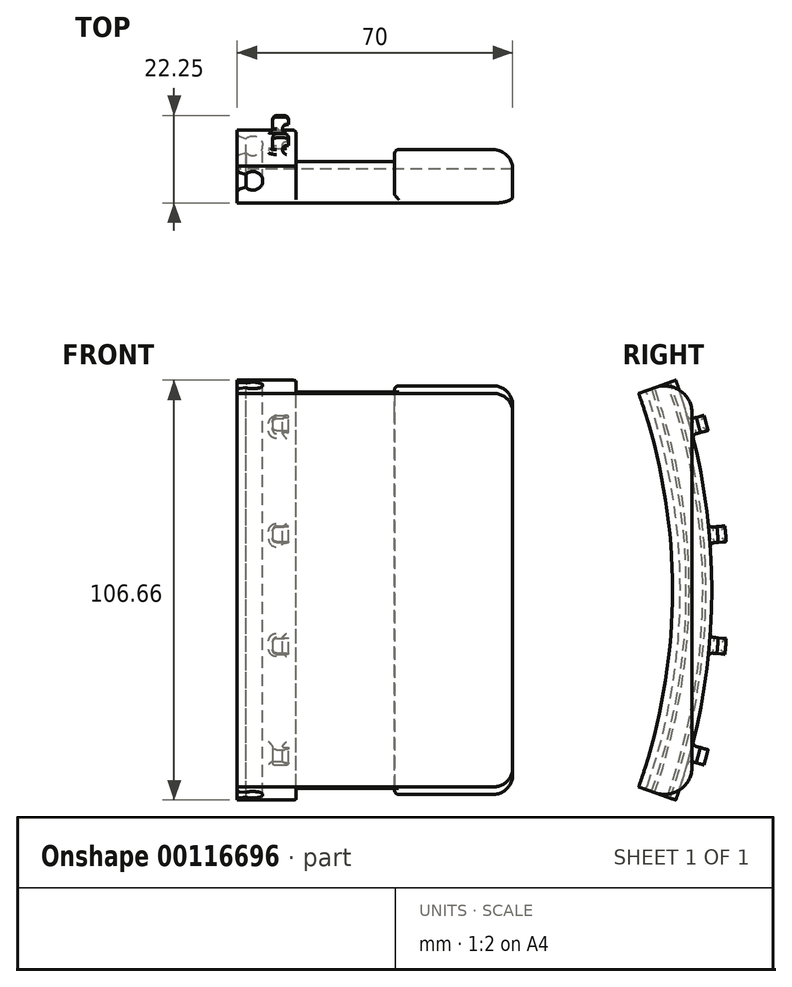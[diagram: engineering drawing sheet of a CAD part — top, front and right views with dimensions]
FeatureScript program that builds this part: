
annotation { "Feature Type Name" : "Feature", "Feature Type Description" : "" }
export const myFeature = defineFeature(function(context is Context, id is Id, definition is map)
    precondition{}
    {
        {
            var Q0;
            Q0=qCreatedBy(makeId("Right.planeOp"),FACE);
            var sketch = newSketch(context, id + "F0", { "sketchPlane" : qUnion([Q0])});
            skArc(sketch, "E0", {"start": v(141.42, -50) * mm, "mid": v(147.84, -25.37) * mm, "end": v(150, 0) * mm});
            skLineSegment(sketch, "E1", {"start": v(155, 0) * mm, "end": v(150, 0) * mm, "construction": true});
            skLineSegment(sketch, "E2", {"start": v(0, 0) * mm, "end": v(141.42, -50) * mm, "construction": true});
            skLineSegment(sketch, "E3", {"start": v(141.42, -50) * mm, "end": v(155, -54.8) * mm});
            skLineSegment(sketch, "E4", {"start": v(155, -54.8) * mm, "end": v(155, 0) * mm});
            skLineSegment(sketch, "E5.MirrorCS", {"start": v(155, 54.8) * mm, "end": v(155, 0) * mm});
            skLineSegment(sketch, "E6.MirrorCS", {"start": v(141.42, 50) * mm, "end": v(155, 54.8) * mm});
            skArc(sketch, "E7.MirrorCS", {"start": v(141.42, 50) * mm, "mid": v(147.84, 25.37) * mm, "end": v(150, 0) * mm});
            skSolve(sketch);
        }
        {
            var Q0;
            Q0 = qSketchRegion(id + "F0", true);
            extrude(context, id + "F1", {"entities" : qUnion([Q0]), "depth" : 30 * mm});
        }
        {
            var Q0;
            Q0=makeQuery(id+"F1.opExtrude","CAP_FACE",FACE,{"disambiguationData":[OSD([sQuery(id+"F0.wireOp",EDGE,"E0"),sQuery(id+"F0.wireOp",EDGE,"E3"),sQuery(id+"F0.wireOp",EDGE,"E4"),sQuery(id+"F0.wireOp",EDGE,"E5.MirrorCS"),sQuery(id+"F0.wireOp",EDGE,"E6.MirrorCS"),sQuery(id+"F0.wireOp",EDGE,"E7.MirrorCS")])],"isStart":true});
            var sketch = newSketch(context, id + "F2", { "sketchPlane" : qUnion([Q0])});
            skArc(sketch, "E8.0", {"start": v(-141.42, -50) * mm, "mid": v(-150, 0) * mm, "end": v(-141.42, 50) * mm});
            skArc(sketch, "E9.0", {"start": v(-143.3, -50.67) * mm, "mid": v(-152, 0) * mm, "end": v(-143.3, 50.67) * mm});
            skLineSegment(sketch, "E10", {"start": v(-141.42, -50) * mm, "end": v(-143.3, -50.67) * mm});
            skLineSegment(sketch, "E11", {"start": v(-141.42, 50) * mm, "end": v(-143.3, 50.67) * mm});
            skSolve(sketch);
        }
        {
            var Q0;
            Q0 = qSketchRegion(id + "F2", true);
            extrude(context, id + "F3", {"entities" : qUnion([Q0]), "operationType" : NewBodyOperationType.ADD, "depth" : 40 * mm});
        }
        {
            var Q0;
            Q0=makeQuery(id+"F3.boolean.opBoolean","MERGE",FACE,{"derivedFrom":[makeQuery(id+"F1.opExtrude","SWEPT_FACE",FACE,{"disambiguationData":[OSD([sQuery(id+"F0.wireOp",EDGE,"E3")])]}),makeQuery(id+"F3.opExtrude","SWEPT_FACE",FACE,{"disambiguationData":[OSD([sQuery(id+"F2.wireOp",EDGE,"E10")])]})]});
            var sketch = newSketch(context, id + "F4", { "sketchPlane" : qUnion([Q0])});
            skLineSegment(sketch, "E12.bottom", {"start": v(-40, -152) * mm, "end": v(-25, -152) * mm});
            skLineSegment(sketch, "E12.top", {"start": v(-40, -160) * mm, "end": v(-31, -160) * mm});
            skLineSegment(sketch, "E12.left", {"start": v(-40, -152) * mm, "end": v(-40, -153.48) * mm});
            skLineSegment(sketch, "E12.right", {"start": v(-25, -152) * mm, "end": v(-25, -160) * mm});
            skArc(sketch, "E13", {"start": v(-37.81, -157.72) * mm, "mid": v(-33.5, -156) * mm, "end": v(-37.81, -154.28) * mm});
            skPoint(sketch, "E13.centerSnap0", {"position": v(-25, -85) * mm});
            skPoint(sketch, "E13.centerSnap1", {"position": v(-40, -156) * mm});
            skLineSegment(sketch, "E14", {"start": v(-37.81, -157.72) * mm, "end": v(-40, -158.52) * mm});
            skLineSegment(sketch, "E15", {"start": v(-36, -156) * mm, "end": v(-40, -156) * mm, "construction": true});
            skLineSegment(sketch, "E16.MirrorCS", {"start": v(-37.81, -154.28) * mm, "end": v(-40, -153.48) * mm});
            skLineSegment(sketch, "E17.trimOffspring", {"start": v(-40, -158.52) * mm, "end": v(-40, -160) * mm});
            skLineSegment(sketch, "E18", {"start": v(-31, -160) * mm, "end": v(-31, -164.13) * mm});
            skLineSegment(sketch, "E19", {"start": v(-31, -164.13) * mm, "end": v(-27, -164.13) * mm});
            skLineSegment(sketch, "E20", {"start": v(-27, -164.13) * mm, "end": v(-27, -162.1) * mm});
            skLineSegment(sketch, "E21", {"start": v(-27, -162.1) * mm, "end": v(-28.5, -162.1) * mm});
            skLineSegment(sketch, "E22", {"start": v(-28.5, -162.1) * mm, "end": v(-28.5, -160) * mm});
            skLineSegment(sketch, "E23.trimOffspring", {"start": v(-28.5, -160) * mm, "end": v(-25, -160) * mm});
            skSolve(sketch);
        }
        {
            var Q0;
            Q0=makeQuery(id+"F4.imprint","IMPRINT",FACE,{"disambiguationData":[TD([[makeQuery(id+"F4.imprint","IMPRINT",EDGE,{"derivedFrom":sQuery(id+"F4.wireOp",EDGE,"E12.bottom")}),-1.0]])]});
            var Q1;
            Q1=makeQuery(id+"F3.opExtrude","CAP_EDGE",EDGE,{"disambiguationData":[OSD([sQuery(id+"F2.wireOp",EDGE,"E9.0")])],"isStart":false});
            sweep(context, id + "F5", {"operationType" : NewBodyOperationType.ADD, "profiles" : qUnion([Q0]), "path" : qUnion([Q1])});
        }
        {
            var Q0;
            Q0=makeQuery(id+"F1.opExtrude","SWEPT_EDGE",EDGE,{"disambiguationData":[OSD([sQuery(id+"F0.wireOp",EDGE,"E3"),sQuery(id+"F0.wireOp",EDGE,"E4")])]});
            var Q1;
            Q1=makeQuery(id+"F1.opExtrude","SWEPT_EDGE",EDGE,{"disambiguationData":[OSD([sQuery(id+"F0.wireOp",EDGE,"E5.MirrorCS"),sQuery(id+"F0.wireOp",EDGE,"E6.MirrorCS")])]});
            fillet(context, id + "F6", {"entities" : qUnion([Q0, Q1]), "radius" : 7 * mm, "tangentPropagation" : true, "allowEdgeOverflow" : false});
        }
        {
            var Q0;
            Q0=qCreatedBy(makeId("Right.planeOp"),FACE);
            cPlane(context, id + "F7", {"entities" : qUnion([Q0]), "cplaneType" : CPlaneType.OFFSET, "offset" : 35 * mm, "oppositeDirection" : true, "width" : 150 * mm, "height" : 150 * mm});
        }
        {
            var Q0;
            Q0=makeQuery(id+"F5.opSweep","SWEPT_FACE",FACE,{"disambiguationData":[OSD([sQuery(id+"F2.wireOp",EDGE,"E9.0"),sQuery(id+"F4.wireOp",EDGE,"E18")])]});
            var sketch = newSketch(context, id + "F8", { "sketchPlane" : qUnion([Q0])});
            skPoint(sketch, "E24.orphan", {"position": v(-150.85, 53.33) * mm});
            skLineSegment(sketch, "E25.MirrorCS", {"start": v(-164.3, 46.1) * mm, "end": v(-160.48, 58.7) * mm});
            skLineSegment(sketch, "E26.MirrorCS", {"start": v(-168.24, 12.71) * mm, "end": v(-159.55, 11.95) * mm});
            skLineSegment(sketch, "E27.MirrorCS", {"start": v(-159.07, 15.92) * mm, "end": v(-167.49, 16.66) * mm});
            skLineSegment(sketch, "E28.MirrorCS", {"start": v(-153.92, 43.31) * mm, "end": v(-164.3, 46.1) * mm});
            skLineSegment(sketch, "E29", {"start": v(0, 0) * mm, "end": v(-188.34, 50.47) * mm, "construction": true});
            skLineSegment(sketch, "E30", {"start": v(0, 0) * mm, "end": v(-190.07, 0) * mm, "construction": true});
            skLineSegment(sketch, "E31", {"start": v(0, 0) * mm, "end": v(-193.8, 16.95) * mm, "construction": true});
            skLineSegment(sketch, "E32", {"start": v(-155.05, 39.48) * mm, "end": v(-164.01, 41.88) * mm});
            skLineSegment(sketch, "E33.trimOffspring", {"start": v(-164.01, 41.88) * mm, "end": v(-167.49, 16.66) * mm});
            skArc(sketch, "E34.0", {"start": v(-150.85, -53.33) * mm, "mid": v(-152.52, -48.36) * mm, "end": v(-154.02, -43.34) * mm});
            skLineSegment(sketch, "E35", {"start": v(-150.85, 53.33) * mm, "end": v(-160.48, 58.7) * mm});
            skArc(sketch, "E36.trimOffspring", {"start": v(-154.02, 43.34) * mm, "mid": v(-152.52, 48.36) * mm, "end": v(-150.85, 53.33) * mm});
            skArc(sketch, "E37.trimOffspring", {"start": v(-159.2, 15.94) * mm, "mid": v(-157.57, 27.78) * mm, "end": v(-155.05, 39.48) * mm});
            skLineSegment(sketch, "E38", {"start": v(-168.24, 12.71) * mm, "end": v(-168.24, 0) * mm});
            skLineSegment(sketch, "E39.MirrorCS", {"start": v(-155.05, -39.48) * mm, "end": v(-164.01, -41.88) * mm});
            skLineSegment(sketch, "E40.MirrorCS", {"start": v(-150.85, -53.33) * mm, "end": v(-160.48, -58.7) * mm});
            skLineSegment(sketch, "E41.MirrorCS", {"start": v(-164.3, -46.1) * mm, "end": v(-160.48, -58.7) * mm});
            skLineSegment(sketch, "E42.MirrorCS", {"start": v(-168.24, -12.71) * mm, "end": v(-159.55, -11.95) * mm});
            skLineSegment(sketch, "E43.MirrorCS", {"start": v(-153.92, -43.31) * mm, "end": v(-164.3, -46.1) * mm});
            skPoint(sketch, "E44.MirrorP", {"position": v(-150.85, -53.33) * mm});
            skArc(sketch, "E45.MirrorCS", {"start": v(-154.02, -43.34) * mm, "mid": v(-152.52, -48.36) * mm, "end": v(-150.85, -53.33) * mm});
            skLineSegment(sketch, "E46.MirrorCS", {"start": v(-168.24, -12.71) * mm, "end": v(-168.24, 0) * mm});
            skLineSegment(sketch, "E47.MirrorCS", {"start": v(-159.07, -15.92) * mm, "end": v(-167.49, -16.66) * mm});
            skArc(sketch, "E48.MirrorCS", {"start": v(-159.2, -15.94) * mm, "mid": v(-157.57, -27.78) * mm, "end": v(-155.05, -39.48) * mm});
            skLineSegment(sketch, "E49.MirrorCS", {"start": v(-164.01, -41.88) * mm, "end": v(-167.49, -16.66) * mm});
            skArc(sketch, "E50.trimOffspring", {"start": v(-159.55, -11.95) * mm, "mid": v(-160, 0) * mm, "end": v(-159.55, 11.95) * mm});
            skArc(sketch, "E51.trimOffspring", {"start": v(-155.05, -39.48) * mm, "mid": v(-157.57, -27.78) * mm, "end": v(-159.2, -15.94) * mm});
            skSolve(sketch);
        }
        {
            var Q0;
            Q0 = qSketchRegion(id + "F8", true);
            var Q1;
            Q1=makeQuery(id+"F5.opSweep","SWEPT_FACE",FACE,{"disambiguationData":[OSD([sQuery(id+"F2.wireOp",EDGE,"E9.0"),sQuery(id+"F4.wireOp",EDGE,"E20")])]});
            extrude(context, id + "F9", {"entities" : qUnion([Q0]), "operationType" : NewBodyOperationType.REMOVE, "endBound" : BoundingType.UP_TO_SURFACE, "oppositeDirection" : true, "endBoundEntityFace" : qUnion([Q1]), "depth" : 25 * mm});
        }
        {
            var Q0;
            {var subQ0=sQuery(id+"F2.wireOp",EDGE,"E9.0");var subQ1=sQuery(id+"F4.wireOp",EDGE,"E18");var subQ2=sQuery(id+"F4.wireOp",EDGE,"E12.top");Q0=makeQuery(id+"F9.boolean.opBoolean","SPLIT",EDGE,{"disambiguationData":[TD([makeQuery(id+"F9.opExtrude","SWEPT_FACE",FACE,{"disambiguationData":[OSD([sQuery(id+"F8.wireOp",EDGE,"E39.MirrorCS")])]})])],"derivedFrom":makeQuery(id+"F5.opSweep","SWEPT_EDGE",EDGE,{"disambiguationData":[OSD([subQ0,subQ2,subQ1])]})});}
            var Q1;
            Q1=makeQuery(id+"F9.boolean.opBoolean","COPY",EDGE,{"derivedFrom":makeQuery(id+"F9.opExtrude","SWEPT_EDGE",EDGE,{"disambiguationData":[OSD([sQuery(id+"F2.wireOp",EDGE,"E9.0"),sQuery(id+"F4.wireOp",EDGE,"E12.top"),sQuery(id+"F4.wireOp",EDGE,"E18"),sQuery(id+"F8.wireOp",EDGE,"E39.MirrorCS"),sQuery(id+"F8.wireOp",EDGE,"E51.trimOffspring")])]})});
            var Q2;
            {var subQ0=sQuery(id+"F2.wireOp",EDGE,"E9.0");var subQ1=sQuery(id+"F4.wireOp",EDGE,"E18");var subQ2=sQuery(id+"F4.wireOp",EDGE,"E12.top");Q2=makeQuery(id+"F9.boolean.opBoolean","SPLIT",EDGE,{"disambiguationData":[TD([makeQuery(id+"F9.opExtrude","SWEPT_FACE",FACE,{"disambiguationData":[OSD([sQuery(id+"F8.wireOp",EDGE,"E42.MirrorCS")])]})])],"derivedFrom":makeQuery(id+"F5.opSweep","SWEPT_EDGE",EDGE,{"disambiguationData":[OSD([subQ0,subQ2,subQ1])]})});}
            var Q3;
            Q3=makeQuery(id+"F9.boolean.opBoolean","COPY",EDGE,{"derivedFrom":makeQuery(id+"F9.opExtrude","SWEPT_EDGE",EDGE,{"disambiguationData":[OSD([sQuery(id+"F2.wireOp",EDGE,"E9.0"),sQuery(id+"F4.wireOp",EDGE,"E12.top"),sQuery(id+"F4.wireOp",EDGE,"E18"),sQuery(id+"F8.wireOp",EDGE,"E42.MirrorCS"),sQuery(id+"F8.wireOp",EDGE,"E50.trimOffspring")])]})});
            var Q4;
            {var subQ0=sQuery(id+"F2.wireOp",EDGE,"E9.0");var subQ1=sQuery(id+"F4.wireOp",EDGE,"E18");var subQ2=sQuery(id+"F4.wireOp",EDGE,"E12.top");Q4=makeQuery(id+"F9.boolean.opBoolean","SPLIT",EDGE,{"disambiguationData":[TD([makeQuery(id+"F9.opExtrude","SWEPT_FACE",FACE,{"disambiguationData":[OSD([sQuery(id+"F8.wireOp",EDGE,"E26.MirrorCS")])]})])],"derivedFrom":makeQuery(id+"F5.opSweep","SWEPT_EDGE",EDGE,{"disambiguationData":[OSD([subQ0,subQ2,subQ1])]})});}
            var Q5;
            Q5=makeQuery(id+"F9.boolean.opBoolean","COPY",EDGE,{"derivedFrom":makeQuery(id+"F9.opExtrude","SWEPT_EDGE",EDGE,{"disambiguationData":[OSD([sQuery(id+"F2.wireOp",EDGE,"E9.0"),sQuery(id+"F4.wireOp",EDGE,"E12.top"),sQuery(id+"F4.wireOp",EDGE,"E18"),sQuery(id+"F8.wireOp",EDGE,"E27.MirrorCS"),sQuery(id+"F8.wireOp",EDGE,"E37.trimOffspring")])]})});
            var Q6;
            {var subQ0=sQuery(id+"F2.wireOp",EDGE,"E9.0");var subQ1=sQuery(id+"F4.wireOp",EDGE,"E18");var subQ2=sQuery(id+"F4.wireOp",EDGE,"E12.top");Q6=makeQuery(id+"F9.boolean.opBoolean","SPLIT",EDGE,{"disambiguationData":[TD([makeQuery(id+"F9.opExtrude","SWEPT_FACE",FACE,{"disambiguationData":[OSD([sQuery(id+"F8.wireOp",EDGE,"E28.MirrorCS")])]})])],"derivedFrom":makeQuery(id+"F5.opSweep","SWEPT_EDGE",EDGE,{"disambiguationData":[OSD([subQ0,subQ2,subQ1])]})});}
            var Q7;
            Q7=makeQuery(id+"F9.boolean.opBoolean","COPY",EDGE,{"derivedFrom":makeQuery(id+"F9.opExtrude","SWEPT_EDGE",EDGE,{"disambiguationData":[OSD([sQuery(id+"F2.wireOp",EDGE,"E9.0"),sQuery(id+"F4.wireOp",EDGE,"E12.top"),sQuery(id+"F4.wireOp",EDGE,"E18"),sQuery(id+"F8.wireOp",EDGE,"E28.MirrorCS"),sQuery(id+"F8.wireOp",EDGE,"E36.trimOffspring")])]})});
            var Q8;
            Q8=makeQuery(id+"F9.boolean.opBoolean","COPY",EDGE,{"derivedFrom":makeQuery(id+"F9.opExtrude","SWEPT_EDGE",EDGE,{"disambiguationData":[OSD([sQuery(id+"F2.wireOp",EDGE,"E9.0"),sQuery(id+"F4.wireOp",EDGE,"E12.top"),sQuery(id+"F4.wireOp",EDGE,"E18"),sQuery(id+"F8.wireOp",EDGE,"E32"),sQuery(id+"F8.wireOp",EDGE,"E37.trimOffspring")])]})});
            var Q9;
            Q9=makeQuery(id+"F9.boolean.opBoolean","COPY",EDGE,{"derivedFrom":makeQuery(id+"F9.opExtrude","CAP_EDGE",EDGE,{"disambiguationData":[OSD([sQuery(id+"F8.wireOp",EDGE,"E26.MirrorCS")])],"isStart":true})});
            var Q10;
            Q10=makeQuery(id+"F9.boolean.opBoolean","COPY",EDGE,{"derivedFrom":makeQuery(id+"F9.opExtrude","SWEPT_EDGE",EDGE,{"disambiguationData":[OSD([sQuery(id+"F2.wireOp",EDGE,"E9.0"),sQuery(id+"F4.wireOp",EDGE,"E12.top"),sQuery(id+"F4.wireOp",EDGE,"E18"),sQuery(id+"F8.wireOp",EDGE,"E47.MirrorCS"),sQuery(id+"F8.wireOp",EDGE,"E51.trimOffspring")])]})});
            var Q11;
            Q11=makeQuery(id+"F9.boolean.opBoolean","COPY",EDGE,{"derivedFrom":makeQuery(id+"F9.opExtrude","SWEPT_EDGE",EDGE,{"disambiguationData":[OSD([sQuery(id+"F2.wireOp",EDGE,"E9.0"),sQuery(id+"F4.wireOp",EDGE,"E12.top"),sQuery(id+"F4.wireOp",EDGE,"E18"),sQuery(id+"F8.wireOp",EDGE,"E43.MirrorCS"),sQuery(id+"F8.wireOp",EDGE,"E45.MirrorCS")])]})});
            var Q12;
            {var subQ0=sQuery(id+"F4.wireOp",EDGE,"E18");var subQ1=sQuery(id+"F2.wireOp",EDGE,"E9.0");var subQ2=sQuery(id+"F4.wireOp",EDGE,"E19");Q12=makeQuery(id+"F9.boolean.opBoolean","SPLIT",EDGE,{"disambiguationData":[TD([makeQuery(id+"F9.opExtrude","SWEPT_FACE",FACE,{"disambiguationData":[OSD([sQuery(id+"F8.wireOp",EDGE,"E39.MirrorCS")])]})])],"derivedFrom":makeQuery(id+"F5.opSweep","SWEPT_EDGE",EDGE,{"disambiguationData":[OSD([subQ1,subQ0,subQ2])]})});}
            var Q13;
            {var subQ0=sQuery(id+"F4.wireOp",EDGE,"E18");var subQ1=sQuery(id+"F2.wireOp",EDGE,"E9.0");var subQ2=sQuery(id+"F4.wireOp",EDGE,"E19");Q13=makeQuery(id+"F9.boolean.opBoolean","SPLIT",EDGE,{"disambiguationData":[TD([makeQuery(id+"F9.opExtrude","SWEPT_FACE",FACE,{"disambiguationData":[OSD([sQuery(id+"F8.wireOp",EDGE,"E42.MirrorCS")])]})])],"derivedFrom":makeQuery(id+"F5.opSweep","SWEPT_EDGE",EDGE,{"disambiguationData":[OSD([subQ1,subQ0,subQ2])]})});}
            var Q14;
            {var subQ0=sQuery(id+"F4.wireOp",EDGE,"E18");var subQ1=sQuery(id+"F2.wireOp",EDGE,"E9.0");var subQ2=sQuery(id+"F4.wireOp",EDGE,"E19");Q14=makeQuery(id+"F9.boolean.opBoolean","SPLIT",EDGE,{"disambiguationData":[TD([makeQuery(id+"F9.opExtrude","SWEPT_FACE",FACE,{"disambiguationData":[OSD([sQuery(id+"F8.wireOp",EDGE,"E26.MirrorCS")])]})])],"derivedFrom":makeQuery(id+"F5.opSweep","SWEPT_EDGE",EDGE,{"disambiguationData":[OSD([subQ1,subQ0,subQ2])]})});}
            var Q15;
            {var subQ0=sQuery(id+"F4.wireOp",EDGE,"E18");var subQ1=sQuery(id+"F2.wireOp",EDGE,"E9.0");var subQ2=sQuery(id+"F4.wireOp",EDGE,"E19");Q15=makeQuery(id+"F9.boolean.opBoolean","SPLIT",EDGE,{"disambiguationData":[TD([makeQuery(id+"F9.opExtrude","SWEPT_FACE",FACE,{"disambiguationData":[OSD([sQuery(id+"F8.wireOp",EDGE,"E28.MirrorCS")])]})])],"derivedFrom":makeQuery(id+"F5.opSweep","SWEPT_EDGE",EDGE,{"disambiguationData":[OSD([subQ1,subQ0,subQ2])]})});}
            var Q16;
            Q16=makeQuery(id+"F9.boolean.opBoolean","COPY",EDGE,{"derivedFrom":makeQuery(id+"F9.opExtrude","CAP_EDGE",EDGE,{"disambiguationData":[OSD([sQuery(id+"F8.wireOp",EDGE,"E32")])],"isStart":true})});
            var Q17;
            Q17=makeQuery(id+"F9.boolean.opBoolean","COPY",EDGE,{"derivedFrom":makeQuery(id+"F9.opExtrude","CAP_EDGE",EDGE,{"disambiguationData":[OSD([sQuery(id+"F8.wireOp",EDGE,"E28.MirrorCS")])],"isStart":true})});
            var Q18;
            Q18=makeQuery(id+"F9.boolean.opBoolean","COPY",EDGE,{"derivedFrom":makeQuery(id+"F9.opExtrude","CAP_EDGE",EDGE,{"disambiguationData":[OSD([sQuery(id+"F8.wireOp",EDGE,"E27.MirrorCS")])],"isStart":true})});
            var Q19;
            Q19=makeQuery(id+"F9.boolean.opBoolean","COPY",EDGE,{"derivedFrom":makeQuery(id+"F9.opExtrude","CAP_EDGE",EDGE,{"disambiguationData":[OSD([sQuery(id+"F8.wireOp",EDGE,"E42.MirrorCS")])],"isStart":true})});
            var Q20;
            Q20=makeQuery(id+"F9.boolean.opBoolean","COPY",EDGE,{"derivedFrom":makeQuery(id+"F9.opExtrude","CAP_EDGE",EDGE,{"disambiguationData":[OSD([sQuery(id+"F8.wireOp",EDGE,"E47.MirrorCS")])],"isStart":true})});
            var Q21;
            Q21=makeQuery(id+"F9.boolean.opBoolean","COPY",EDGE,{"derivedFrom":makeQuery(id+"F9.opExtrude","CAP_EDGE",EDGE,{"disambiguationData":[OSD([sQuery(id+"F8.wireOp",EDGE,"E43.MirrorCS")])],"isStart":true})});
            var Q22;
            Q22=makeQuery(id+"F9.boolean.opBoolean","COPY",EDGE,{"derivedFrom":makeQuery(id+"F9.opExtrude","CAP_EDGE",EDGE,{"disambiguationData":[OSD([sQuery(id+"F8.wireOp",EDGE,"E39.MirrorCS")])],"isStart":true})});
            var Q23;
            {var subQ0=sQuery(id+"F4.wireOp",EDGE,"E19");var subQ1=sQuery(id+"F2.wireOp",EDGE,"E9.0");var subQ2=sQuery(id+"F4.wireOp",EDGE,"E20");Q23=makeQuery(id+"F9.boolean.opBoolean","SPLIT",EDGE,{"disambiguationData":[TD([makeQuery(id+"F9.opExtrude","SWEPT_FACE",FACE,{"disambiguationData":[OSD([sQuery(id+"F8.wireOp",EDGE,"E39.MirrorCS")])]})])],"derivedFrom":makeQuery(id+"F5.opSweep","SWEPT_EDGE",EDGE,{"disambiguationData":[OSD([subQ1,subQ0,subQ2])]})});}
            var Q24;
            {var subQ0=sQuery(id+"F4.wireOp",EDGE,"E21");var subQ1=sQuery(id+"F2.wireOp",EDGE,"E9.0");var subQ2=sQuery(id+"F4.wireOp",EDGE,"E22");Q24=makeQuery(id+"F9.boolean.opBoolean","SPLIT",EDGE,{"disambiguationData":[TD([makeQuery(id+"F9.opExtrude","SWEPT_FACE",FACE,{"disambiguationData":[OSD([sQuery(id+"F8.wireOp",EDGE,"E39.MirrorCS")])]})])],"derivedFrom":makeQuery(id+"F5.opSweep","SWEPT_EDGE",EDGE,{"disambiguationData":[OSD([subQ1,subQ0,subQ2])]})});}
            var Q25;
            {var subQ0=sQuery(id+"F4.wireOp",EDGE,"E21");var subQ1=sQuery(id+"F2.wireOp",EDGE,"E9.0");var subQ2=sQuery(id+"F4.wireOp",EDGE,"E22");Q25=makeQuery(id+"F9.boolean.opBoolean","SPLIT",EDGE,{"disambiguationData":[TD([makeQuery(id+"F9.opExtrude","SWEPT_FACE",FACE,{"disambiguationData":[OSD([sQuery(id+"F8.wireOp",EDGE,"E42.MirrorCS")])]})])],"derivedFrom":makeQuery(id+"F5.opSweep","SWEPT_EDGE",EDGE,{"disambiguationData":[OSD([subQ1,subQ0,subQ2])]})});}
            var Q26;
            {var subQ0=sQuery(id+"F4.wireOp",EDGE,"E19");var subQ1=sQuery(id+"F2.wireOp",EDGE,"E9.0");var subQ2=sQuery(id+"F4.wireOp",EDGE,"E20");Q26=makeQuery(id+"F9.boolean.opBoolean","SPLIT",EDGE,{"disambiguationData":[TD([makeQuery(id+"F9.opExtrude","SWEPT_FACE",FACE,{"disambiguationData":[OSD([sQuery(id+"F8.wireOp",EDGE,"E42.MirrorCS")])]})])],"derivedFrom":makeQuery(id+"F5.opSweep","SWEPT_EDGE",EDGE,{"disambiguationData":[OSD([subQ1,subQ0,subQ2])]})});}
            var Q27;
            {var subQ0=sQuery(id+"F4.wireOp",EDGE,"E21");var subQ1=sQuery(id+"F2.wireOp",EDGE,"E9.0");var subQ2=sQuery(id+"F4.wireOp",EDGE,"E22");Q27=makeQuery(id+"F9.boolean.opBoolean","SPLIT",EDGE,{"disambiguationData":[TD([makeQuery(id+"F9.opExtrude","SWEPT_FACE",FACE,{"disambiguationData":[OSD([sQuery(id+"F8.wireOp",EDGE,"E26.MirrorCS")])]})])],"derivedFrom":makeQuery(id+"F5.opSweep","SWEPT_EDGE",EDGE,{"disambiguationData":[OSD([subQ1,subQ0,subQ2])]})});}
            var Q28;
            {var subQ0=sQuery(id+"F4.wireOp",EDGE,"E19");var subQ1=sQuery(id+"F2.wireOp",EDGE,"E9.0");var subQ2=sQuery(id+"F4.wireOp",EDGE,"E20");Q28=makeQuery(id+"F9.boolean.opBoolean","SPLIT",EDGE,{"disambiguationData":[TD([makeQuery(id+"F9.opExtrude","SWEPT_FACE",FACE,{"disambiguationData":[OSD([sQuery(id+"F8.wireOp",EDGE,"E26.MirrorCS")])]})])],"derivedFrom":makeQuery(id+"F5.opSweep","SWEPT_EDGE",EDGE,{"disambiguationData":[OSD([subQ1,subQ0,subQ2])]})});}
            var Q29;
            {var subQ0=sQuery(id+"F4.wireOp",EDGE,"E21");var subQ1=sQuery(id+"F2.wireOp",EDGE,"E9.0");var subQ2=sQuery(id+"F4.wireOp",EDGE,"E22");Q29=makeQuery(id+"F9.boolean.opBoolean","SPLIT",EDGE,{"disambiguationData":[TD([makeQuery(id+"F9.opExtrude","SWEPT_FACE",FACE,{"disambiguationData":[OSD([sQuery(id+"F8.wireOp",EDGE,"E28.MirrorCS")])]})])],"derivedFrom":makeQuery(id+"F5.opSweep","SWEPT_EDGE",EDGE,{"disambiguationData":[OSD([subQ1,subQ0,subQ2])]})});}
            var Q30;
            {var subQ0=sQuery(id+"F4.wireOp",EDGE,"E19");var subQ1=sQuery(id+"F2.wireOp",EDGE,"E9.0");var subQ2=sQuery(id+"F4.wireOp",EDGE,"E20");Q30=makeQuery(id+"F9.boolean.opBoolean","SPLIT",EDGE,{"disambiguationData":[TD([makeQuery(id+"F9.opExtrude","SWEPT_FACE",FACE,{"disambiguationData":[OSD([sQuery(id+"F8.wireOp",EDGE,"E28.MirrorCS")])]})])],"derivedFrom":makeQuery(id+"F5.opSweep","SWEPT_EDGE",EDGE,{"disambiguationData":[OSD([subQ1,subQ0,subQ2])]})});}
            var Q31;
            Q31=makeQuery(id+"F5.opSweep","SWEPT_EDGE",EDGE,{"disambiguationData":[OSD([sQuery(id+"F2.wireOp",EDGE,"E9.0"),sQuery(id+"F4.wireOp",EDGE,"E12.right"),sQuery(id+"F4.wireOp",EDGE,"E23.trimOffspring")])]});
            var Q32;
            Q32=makeQuery(id+"F1.opExtrude","CAP_EDGE",EDGE,{"disambiguationData":[OSD([sQuery(id+"F0.wireOp",EDGE,"E4"),sQuery(id+"F0.wireOp",EDGE,"E5.MirrorCS")])],"isStart":true});
            var Q33;
            Q33=makeQuery(id+"F3.opExtrude","SWEPT_EDGE",EDGE,{"disambiguationData":[OSD([sQuery(id+"F0.wireOp",EDGE,"E3"),sQuery(id+"F2.wireOp",EDGE,"E9.0"),sQuery(id+"F2.wireOp",EDGE,"E10")])]});
            var Q34;
            Q34=makeQuery(id+"F3.opExtrude","SWEPT_EDGE",EDGE,{"disambiguationData":[OSD([sQuery(id+"F0.wireOp",EDGE,"E6.MirrorCS"),sQuery(id+"F2.wireOp",EDGE,"E9.0"),sQuery(id+"F2.wireOp",EDGE,"E11")])]});
            fillet(context, id + "F10", {"entities" : qUnion([Q0, Q1, Q2, Q3, Q4, Q5, Q6, Q7, Q8, Q9, Q10, Q11, Q12, Q13, Q14, Q15, Q16, Q17, Q18, Q19, Q20, Q21, Q22, Q23, Q24, Q25, Q26, Q27, Q28, Q29, Q30, Q31, Q32, Q33, Q34]), "radius" : 1 * mm, "tangentPropagation" : true, "allowEdgeOverflow" : false});
        }
        {
            var Q0;
            Q0=makeQuery(id+"F5.opSweep","SWEPT_EDGE",EDGE,{"disambiguationData":[OSD([sQuery(id+"F2.wireOp",EDGE,"E9.0"),sQuery(id+"F4.wireOp",EDGE,"E12.left"),sQuery(id+"F4.wireOp",EDGE,"E16.MirrorCS")])]});
            var Q1;
            Q1=makeQuery(id+"F5.opSweep","SWEPT_EDGE",EDGE,{"disambiguationData":[OSD([sQuery(id+"F2.wireOp",EDGE,"E9.0"),sQuery(id+"F4.wireOp",EDGE,"E14"),sQuery(id+"F4.wireOp",EDGE,"E17.trimOffspring")])]});
            fillet(context, id + "F11", {"entities" : qUnion([Q0, Q1]), "radius" : 1 * mm, "tangentPropagation" : true, "allowEdgeOverflow" : false});
        }
        {
            var Q0;
            {var subQ0=sQuery(id+"F4.wireOp",EDGE,"E23.trimOffspring");var subQ1=sQuery(id+"F2.wireOp",EDGE,"E9.0");var subQ2=sQuery(id+"F4.wireOp",EDGE,"E22");Q0=makeQuery(id+"F9.boolean.opBoolean","SPLIT",EDGE,{"disambiguationData":[TD([makeQuery(id+"F9.opExtrude","SWEPT_FACE",FACE,{"disambiguationData":[OSD([sQuery(id+"F8.wireOp",EDGE,"E39.MirrorCS")])]})])],"derivedFrom":makeQuery(id+"F5.opSweep","SWEPT_EDGE",EDGE,{"disambiguationData":[OSD([subQ1,subQ2,subQ0])]})});}
            var Q1;
            {var subQ0=sQuery(id+"F4.wireOp",EDGE,"E23.trimOffspring");var subQ1=sQuery(id+"F2.wireOp",EDGE,"E9.0");var subQ2=sQuery(id+"F4.wireOp",EDGE,"E22");Q1=makeQuery(id+"F9.boolean.opBoolean","SPLIT",EDGE,{"disambiguationData":[TD([makeQuery(id+"F9.opExtrude","SWEPT_FACE",FACE,{"disambiguationData":[OSD([sQuery(id+"F8.wireOp",EDGE,"E42.MirrorCS")])]})])],"derivedFrom":makeQuery(id+"F5.opSweep","SWEPT_EDGE",EDGE,{"disambiguationData":[OSD([subQ1,subQ2,subQ0])]})});}
            var Q2;
            {var subQ0=sQuery(id+"F4.wireOp",EDGE,"E23.trimOffspring");var subQ1=sQuery(id+"F2.wireOp",EDGE,"E9.0");var subQ2=sQuery(id+"F4.wireOp",EDGE,"E22");Q2=makeQuery(id+"F9.boolean.opBoolean","SPLIT",EDGE,{"disambiguationData":[TD([makeQuery(id+"F9.opExtrude","SWEPT_FACE",FACE,{"disambiguationData":[OSD([sQuery(id+"F8.wireOp",EDGE,"E26.MirrorCS")])]})])],"derivedFrom":makeQuery(id+"F5.opSweep","SWEPT_EDGE",EDGE,{"disambiguationData":[OSD([subQ1,subQ2,subQ0])]})});}
            var Q3;
            {var subQ0=sQuery(id+"F4.wireOp",EDGE,"E23.trimOffspring");var subQ1=sQuery(id+"F2.wireOp",EDGE,"E9.0");var subQ2=sQuery(id+"F4.wireOp",EDGE,"E22");Q3=makeQuery(id+"F9.boolean.opBoolean","SPLIT",EDGE,{"disambiguationData":[TD([makeQuery(id+"F9.opExtrude","SWEPT_FACE",FACE,{"disambiguationData":[OSD([sQuery(id+"F8.wireOp",EDGE,"E28.MirrorCS")])]})])],"derivedFrom":makeQuery(id+"F5.opSweep","SWEPT_EDGE",EDGE,{"disambiguationData":[OSD([subQ1,subQ2,subQ0])]})});}
            fillet(context, id + "F12", {"entities" : qUnion([Q0, Q1, Q2, Q3]), "radius" : 1 * mm, "tangentPropagation" : true, "allowEdgeOverflow" : false});
        }
        {
            var Q0;
            Q0=makeQuery(id+"F1.opExtrude","CAP_EDGE",EDGE,{"disambiguationData":[OSD([sQuery(id+"F0.wireOp",EDGE,"E4"),sQuery(id+"F0.wireOp",EDGE,"E5.MirrorCS")])],"isStart":false});
            fillet(context, id + "F13", {"entities" : qUnion([Q0]), "radius" : 5 * mm, "tangentPropagation" : true, "allowEdgeOverflow" : false});
        }
    });
